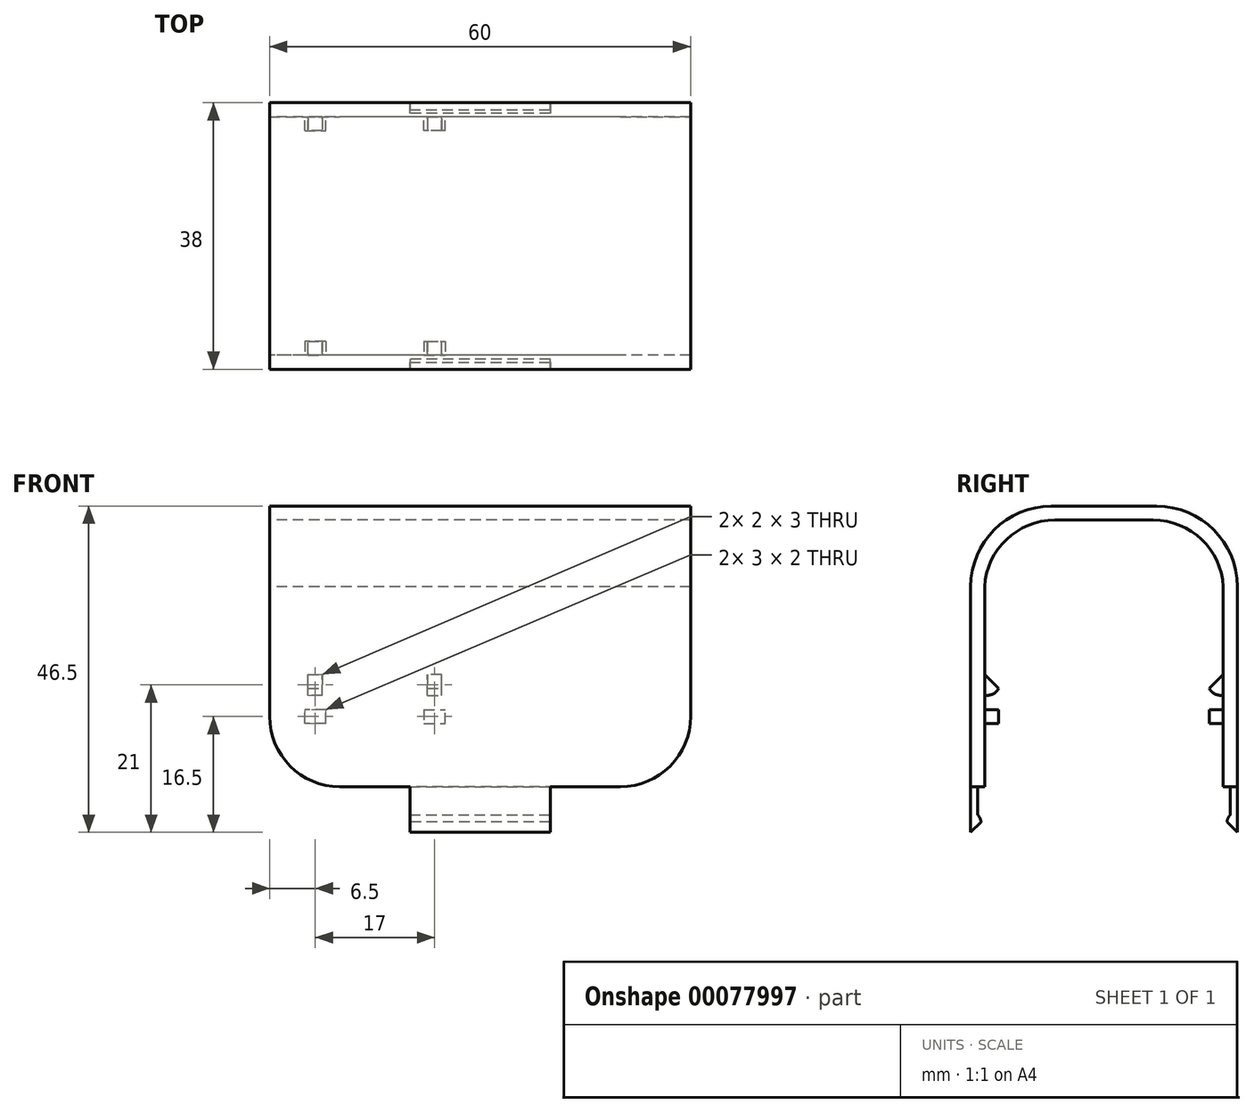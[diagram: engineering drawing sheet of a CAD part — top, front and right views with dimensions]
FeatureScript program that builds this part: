
annotation { "Feature Type Name" : "Feature", "Feature Type Description" : "" }
export const myFeature = defineFeature(function(context is Context, id is Id, definition is map)
    precondition{}
    {
        {
            var Q0;
            Q0=qCreatedBy(makeId("Right.planeOp"),FACE);
            var sketch = newSketch(context, id + "F0", { "sketchPlane" : qUnion([Q0])});
            skLineSegment(sketch, "E0", {"start": v(0, 0) * mm, "end": v(0, 28.5) * mm});
            skLineSegment(sketch, "E1", {"start": v(-11.5, 40) * mm, "end": v(-26.5, 40) * mm});
            skLineSegment(sketch, "E2", {"start": v(-38, 28.5) * mm, "end": v(-38, 0) * mm});
            skPoint(sketch, "E3.visualSharp", {"position": v(0, 40) * mm});
            skArc(sketch, "E3.filletArc", {"start": v(0, 28.5) * mm, "mid": v(-3.37, 36.63) * mm, "end": v(-11.5, 40) * mm});
            skPoint(sketch, "E4.visualSharp", {"position": v(-38, 40) * mm});
            skArc(sketch, "E4.filletArc", {"start": v(-26.5, 40) * mm, "mid": v(-34.63, 36.63) * mm, "end": v(-38, 28.5) * mm});
            skLineSegment(sketch, "E5.0", {"start": v(-36, 28.5) * mm, "end": v(-36, 0) * mm});
            skLineSegment(sketch, "E5.1", {"start": v(-2, 0) * mm, "end": v(-2, 28.5) * mm});
            skLineSegment(sketch, "E5.3", {"start": v(-11.99, 38) * mm, "end": v(-26.01, 38) * mm});
            skLineSegment(sketch, "E6", {"start": v(-38, 0) * mm, "end": v(-36, 0) * mm});
            skLineSegment(sketch, "E7", {"start": v(-2, 0) * mm, "end": v(0, 0) * mm});
            skArc(sketch, "E8", {"start": v(-2, 28.5) * mm, "mid": v(-5.1, 35.25) * mm, "end": v(-11.99, 38) * mm});
            skArc(sketch, "E9", {"start": v(-26.01, 38) * mm, "mid": v(-32.9, 35.25) * mm, "end": v(-36, 28.5) * mm});
            skSolve(sketch);
        }
        {
            var Q0;
            Q0=qSketchRegion(id+"F0",true);
            extrude(context, id + "F1", {"entities" : qUnion([Q0]), "endBound" : BoundingType.SYMMETRIC, "depth" : 60 * mm});
        }
        {
            var Q0;
            Q0=makeQuery(id+"F1.opExtrude","CAP_EDGE",EDGE,{"disambiguationData":[OSD([sQuery(id+"F0.wireOp",EDGE,"E6")])],"isStart":false});
            var Q1;
            Q1=makeQuery(id+"F1.opExtrude","CAP_EDGE",EDGE,{"disambiguationData":[OSD([sQuery(id+"F0.wireOp",EDGE,"E7")])],"isStart":false});
            var Q2;
            Q2=makeQuery(id+"F1.opExtrude","CAP_EDGE",EDGE,{"disambiguationData":[OSD([sQuery(id+"F0.wireOp",EDGE,"E7")])],"isStart":true});
            var Q3;
            Q3=makeQuery(id+"F1.opExtrude","CAP_EDGE",EDGE,{"disambiguationData":[OSD([sQuery(id+"F0.wireOp",EDGE,"E6")])],"isStart":true});
            fillet(context, id + "F2", {"entities" : qUnion([Q0, Q1, Q2, Q3]), "radius" : 10 * mm, "tangentPropagation" : true, "allowEdgeOverflow" : false});
        }
        {
            var Q0;
            Q0=makeQuery(id+"F1.opExtrude","SWEPT_FACE",FACE,{"disambiguationData":[OSD([sQuery(id+"F0.wireOp",EDGE,"E6")])]});
            var sketch = newSketch(context, id + "F3", { "sketchPlane" : qUnion([Q0])});
            skLineSegment(sketch, "E10", {"start": v(-20, 38) * mm, "end": v(-10, 38) * mm, "construction": true});
            skLineSegment(sketch, "E11", {"start": v(20, 38) * mm, "end": v(10, 38) * mm, "construction": true});
            skLineSegment(sketch, "E12", {"start": v(-10, 38) * mm, "end": v(-10, 0) * mm, "construction": true});
            skLineSegment(sketch, "E13", {"start": v(10, 38) * mm, "end": v(10, 0) * mm, "construction": true});
            skLineSegment(sketch, "E14", {"start": v(-10, 38) * mm, "end": v(10, 38) * mm});
            skLineSegment(sketch, "E15", {"start": v(-10, 0) * mm, "end": v(10, 0) * mm});
            skLineSegment(sketch, "E16", {"start": v(-10, 38) * mm, "end": v(-10, 37) * mm});
            skLineSegment(sketch, "E17", {"start": v(-10, 37) * mm, "end": v(10, 37) * mm});
            skLineSegment(sketch, "E18", {"start": v(10, 37) * mm, "end": v(10, 38) * mm});
            skLineSegment(sketch, "E19", {"start": v(-10, 0) * mm, "end": v(-10, 1) * mm});
            skLineSegment(sketch, "E20", {"start": v(-10, 1) * mm, "end": v(10, 1) * mm});
            skLineSegment(sketch, "E21", {"start": v(10, 1) * mm, "end": v(10, 0) * mm});
            skSolve(sketch);
        }
        {
            var Q0;
            Q0=makeQuery(id+"F3.imprint","IMPRINT",FACE,{"disambiguationData":[TD([[makeQuery(id+"F3.imprint","IMPRINT",EDGE,{"derivedFrom":sQuery(id+"F3.wireOp",EDGE,"E15")}),1.0]])]});
            var Q1;
            Q1=makeQuery(id+"F3.imprint","IMPRINT",FACE,{"disambiguationData":[TD([[makeQuery(id+"F3.imprint","IMPRINT",EDGE,{"derivedFrom":sQuery(id+"F3.wireOp",EDGE,"E14")}),1.0]])]});
            extrude(context, id + "F4", {"entities" : qUnion([Q0, Q1]), "operationType" : NewBodyOperationType.ADD, "depth" : 4 * mm});
        }
        {
            var Q0;
            Q0=makeQuery(id+"F4.opExtrude","CAP_FACE",FACE,{"disambiguationData":[OSD([sQuery(id+"F3.wireOp",EDGE,"E14"),sQuery(id+"F3.wireOp",EDGE,"E16"),sQuery(id+"F3.wireOp",EDGE,"E17"),sQuery(id+"F3.wireOp",EDGE,"E18")])],"isStart":false});
            var sketch = newSketch(context, id + "F5", { "sketchPlane" : qUnion([Q0])});
            skLineSegment(sketch, "E22", {"start": v(-10, 38) * mm, "end": v(-10, 36.5) * mm});
            skLineSegment(sketch, "E23", {"start": v(-10, 36.5) * mm, "end": v(9.99, 36.5) * mm});
            skLineSegment(sketch, "E24", {"start": v(9.99, 36.5) * mm, "end": v(10, 38) * mm});
            skLineSegment(sketch, "E25", {"start": v(-10, 38) * mm, "end": v(10, 38) * mm});
            skLineSegment(sketch, "E26.MirrorCS", {"start": v(-10, 0) * mm, "end": v(-10, 1.5) * mm});
            skLineSegment(sketch, "E27.MirrorCS", {"start": v(9.99, 1.5) * mm, "end": v(10, 0) * mm});
            skLineSegment(sketch, "E28.MirrorCS", {"start": v(-10, 1.5) * mm, "end": v(9.99, 1.5) * mm});
            skLineSegment(sketch, "E29.MirrorCS", {"start": v(-10, 0) * mm, "end": v(10, 0) * mm});
            skSolve(sketch);
        }
        {
            var Q0;
            Q0=qSketchRegion(id+"F5",true);
            extrude(context, id + "F6", {"entities" : qUnion([Q0]), "operationType" : NewBodyOperationType.ADD, "depth" : 3 * mm});
        }
        {
            var Q0;
            Q0=makeQuery(id+"F6.opExtrude","CAP_EDGE",EDGE,{"disambiguationData":[OSD([sQuery(id+"F5.wireOp",EDGE,"E28.MirrorCS")])],"isStart":true});
            var Q1;
            Q1=makeQuery(id+"F6.opExtrude","CAP_EDGE",EDGE,{"disambiguationData":[OSD([sQuery(id+"F5.wireOp",EDGE,"E23")])],"isStart":true});
            fillet(context, id + "F7", {"entities" : qUnion([Q0, Q1]), "radius" : 2 * mm, "tangentPropagation" : true, "allowEdgeOverflow" : false});
        }
        {
            var Q0;
            Q0=makeQuery(id+"F6.opExtrude","CAP_EDGE",EDGE,{"disambiguationData":[OSD([sQuery(id+"F5.wireOp",EDGE,"E28.MirrorCS")])],"isStart":false});
            var Q1;
            Q1=makeQuery(id+"F6.opExtrude","CAP_EDGE",EDGE,{"disambiguationData":[OSD([sQuery(id+"F5.wireOp",EDGE,"E23")])],"isStart":false});
            chamfer(context, id + "F8", {"entities" : qUnion([Q0, Q1]), "width" : 2 * mm, "tangentPropagation" : true});
        }
        {
            var Q0;
            Q0=makeQuery(id+"F1.opExtrude","SWEPT_FACE",FACE,{"disambiguationData":[OSD([sQuery(id+"F0.wireOp",EDGE,"E5.1")])]});
            var sketch = newSketch(context, id + "F9", { "sketchPlane" : qUnion([Q0])});
            skLineSegment(sketch, "E30", {"start": v(-20, 0) * mm, "end": v(-30, 0) * mm, "construction": true});
            skLineSegment(sketch, "E31", {"start": v(-25, 10) * mm, "end": v(-25, 11) * mm});
            skLineSegment(sketch, "E32", {"start": v(-25, 11) * mm, "end": v(-22, 11) * mm});
            skLineSegment(sketch, "E33", {"start": v(-25, 10) * mm, "end": v(-25, 9) * mm});
            skLineSegment(sketch, "E34", {"start": v(-25, 9) * mm, "end": v(-22, 9) * mm});
            skLineSegment(sketch, "E35", {"start": v(-22, 9) * mm, "end": v(-22, 11) * mm});
            skLineSegment(sketch, "E36", {"start": v(-25, 11) * mm, "end": v(-25, 13) * mm, "construction": true});
            skLineSegment(sketch, "E37", {"start": v(-30, 10) * mm, "end": v(-30, 6.48) * mm, "construction": true});
            skLineSegment(sketch, "E38", {"start": v(-24.5, 13) * mm, "end": v(-22.5, 13) * mm});
            skLineSegment(sketch, "E39", {"start": v(-22.5, 13) * mm, "end": v(-22.5, 16) * mm});
            skLineSegment(sketch, "E40", {"start": v(-22.5, 16) * mm, "end": v(-24.5, 16) * mm});
            skLineSegment(sketch, "E41", {"start": v(-24.5, 13) * mm, "end": v(-24.5, 16) * mm});
            skLineSegment(sketch, "E42", {"start": v(-25, 13) * mm, "end": v(-24.5, 13) * mm, "construction": true});
            skLineSegment(sketch, "E43", {"start": v(-15, 9) * mm, "end": v(-15, 3.17) * mm, "construction": true});
            skLineSegment(sketch, "E44.MirrorCS", {"start": v(-5, 11) * mm, "end": v(-5, 13) * mm, "construction": true});
            skLineSegment(sketch, "E45.MirrorCS", {"start": v(-5, 13) * mm, "end": v(-5.5, 13) * mm, "construction": true});
            skLineSegment(sketch, "E46.MirrorCS", {"start": v(-5, 10) * mm, "end": v(-5, 9) * mm});
            skLineSegment(sketch, "E47.MirrorCS", {"start": v(-5, 10) * mm, "end": v(-5, 11) * mm});
            skLineSegment(sketch, "E48.MirrorCS", {"start": v(-7.5, 16) * mm, "end": v(-5.5, 16) * mm});
            skLineSegment(sketch, "E49.MirrorCS", {"start": v(-5.5, 13) * mm, "end": v(-7.5, 13) * mm});
            skLineSegment(sketch, "E50.MirrorCS", {"start": v(-7.5, 13) * mm, "end": v(-7.5, 16) * mm});
            skLineSegment(sketch, "E51.MirrorCS", {"start": v(-5.5, 13) * mm, "end": v(-5.5, 16) * mm});
            skLineSegment(sketch, "E52.MirrorCS", {"start": v(-5, 11) * mm, "end": v(-8, 11) * mm});
            skLineSegment(sketch, "E53.MirrorCS", {"start": v(-5, 9) * mm, "end": v(-8, 9) * mm});
            skLineSegment(sketch, "E54.MirrorCS", {"start": v(-8, 9) * mm, "end": v(-8, 11) * mm});
            skSolve(sketch);
        }
        {
            var Q0;
            Q0=makeQuery(id+"F1.opExtrude","SWEPT_FACE",FACE,{"disambiguationData":[OSD([sQuery(id+"F0.wireOp",EDGE,"E5.0")])]});
            var sketch = newSketch(context, id + "F10", { "sketchPlane" : qUnion([Q0])});
            skLineSegment(sketch, "E55", {"start": v(30, 0) * mm, "end": v(20, 0) * mm, "construction": true});
            skLineSegment(sketch, "E56", {"start": v(22, 10) * mm, "end": v(22, 11) * mm});
            skLineSegment(sketch, "E57", {"start": v(22, 11) * mm, "end": v(25, 11) * mm});
            skLineSegment(sketch, "E58", {"start": v(22, 10) * mm, "end": v(22, 9) * mm});
            skLineSegment(sketch, "E59", {"start": v(22, 9) * mm, "end": v(25, 9) * mm});
            skLineSegment(sketch, "E60", {"start": v(25, 9) * mm, "end": v(25, 11) * mm});
            skLineSegment(sketch, "E61", {"start": v(22, 11) * mm, "end": v(22, 13) * mm, "construction": true});
            skLineSegment(sketch, "E62", {"start": v(22.5, 13) * mm, "end": v(24.5, 13) * mm});
            skLineSegment(sketch, "E63", {"start": v(24.5, 13) * mm, "end": v(24.5, 16) * mm});
            skLineSegment(sketch, "E64", {"start": v(24.5, 16) * mm, "end": v(22.5, 16) * mm});
            skLineSegment(sketch, "E65", {"start": v(22.5, 13) * mm, "end": v(22.5, 16) * mm});
            skLineSegment(sketch, "E66", {"start": v(22, 13) * mm, "end": v(22.5, 13) * mm, "construction": true});
            skLineSegment(sketch, "E67", {"start": v(20, 0) * mm, "end": v(30, 0) * mm, "construction": true});
            skLineSegment(sketch, "E68", {"start": v(30, 0) * mm, "end": v(30, 11) * mm, "construction": true});
            skLineSegment(sketch, "E69", {"start": v(30, 11) * mm, "end": v(25, 11) * mm, "construction": true});
            skLineSegment(sketch, "E70", {"start": v(15, 9) * mm, "end": v(15, 1.98) * mm, "construction": true});
            skLineSegment(sketch, "E71.MirrorCS", {"start": v(8, 11) * mm, "end": v(8, 13) * mm, "construction": true});
            skLineSegment(sketch, "E72.MirrorCS", {"start": v(8, 13) * mm, "end": v(7.5, 13) * mm, "construction": true});
            skLineSegment(sketch, "E73.MirrorCS", {"start": v(8, 10) * mm, "end": v(8, 9) * mm});
            skLineSegment(sketch, "E74.MirrorCS", {"start": v(8, 10) * mm, "end": v(8, 11) * mm});
            skLineSegment(sketch, "E75.MirrorCS", {"start": v(5.5, 13) * mm, "end": v(5.5, 16) * mm});
            skLineSegment(sketch, "E76.MirrorCS", {"start": v(7.5, 13) * mm, "end": v(7.5, 16) * mm});
            skLineSegment(sketch, "E77.MirrorCS", {"start": v(5.5, 16) * mm, "end": v(7.5, 16) * mm});
            skLineSegment(sketch, "E78.MirrorCS", {"start": v(7.5, 13) * mm, "end": v(5.5, 13) * mm});
            skLineSegment(sketch, "E79.MirrorCS", {"start": v(5, 9) * mm, "end": v(5, 11) * mm});
            skLineSegment(sketch, "E80.MirrorCS", {"start": v(8, 9) * mm, "end": v(5, 9) * mm});
            skLineSegment(sketch, "E81.MirrorCS", {"start": v(8, 11) * mm, "end": v(5, 11) * mm});
            skSolve(sketch);
        }
        {
            var Q0;
            Q0=makeQuery(id+"F9.imprint","IMPRINT",FACE,{"disambiguationData":[TD([[makeQuery(id+"F9.imprint","IMPRINT",EDGE,{"derivedFrom":sQuery(id+"F9.wireOp",EDGE,"E31")}),-1.0]])]});
            var Q1;
            Q1=makeQuery(id+"F9.imprint","IMPRINT",FACE,{"disambiguationData":[TD([[makeQuery(id+"F9.imprint","IMPRINT",EDGE,{"derivedFrom":sQuery(id+"F9.wireOp",EDGE,"E38")}),1.0]])]});
            var Q2;
            Q2=makeQuery(id+"F9.imprint","IMPRINT",FACE,{"disambiguationData":[TD([[makeQuery(id+"F9.imprint","IMPRINT",EDGE,{"derivedFrom":sQuery(id+"F9.wireOp",EDGE,"E46.MirrorCS")}),-1.0]])]});
            var Q3;
            Q3=makeQuery(id+"F9.imprint","IMPRINT",FACE,{"disambiguationData":[TD([[makeQuery(id+"F9.imprint","IMPRINT",EDGE,{"derivedFrom":sQuery(id+"F9.wireOp",EDGE,"E48.MirrorCS")}),-1.0]])]});
            extrude(context, id + "F11", {"entities" : qUnion([Q0, Q1, Q2, Q3]), "operationType" : NewBodyOperationType.ADD, "depth" : 2 * mm});
        }
        {
            var Q0;
            Q0=qSketchRegion(id+"F10",true);
            extrude(context, id + "F12", {"entities" : qUnion([Q0]), "operationType" : NewBodyOperationType.ADD, "depth" : 2 * mm});
        }
        {
            var Q0;
            Q0=makeQuery(id+"F11.opExtrude","CAP_EDGE",EDGE,{"disambiguationData":[OSD([sQuery(id+"F9.wireOp",EDGE,"E40")])],"isStart":false});
            var Q1;
            Q1=makeQuery(id+"F12.opExtrude","CAP_EDGE",EDGE,{"disambiguationData":[OSD([sQuery(id+"F10.wireOp",EDGE,"E64")])],"isStart":false});
            var Q2;
            Q2=makeQuery(id+"F11.opExtrude","CAP_EDGE",EDGE,{"disambiguationData":[OSD([sQuery(id+"F9.wireOp",EDGE,"E48.MirrorCS")])],"isStart":false});
            var Q3;
            Q3=makeQuery(id+"F12.opExtrude","CAP_EDGE",EDGE,{"disambiguationData":[OSD([sQuery(id+"F10.wireOp",EDGE,"E77.MirrorCS")])],"isStart":false});
            chamfer(context, id + "F13", {"entities" : qUnion([Q0, Q1, Q2, Q3]), "width" : 2 * mm, "tangentPropagation" : true});
        }
        {
            var Q0;
            Q0=makeQuery(id+"F11.opExtrude","CAP_EDGE",EDGE,{"disambiguationData":[OSD([sQuery(id+"F9.wireOp",EDGE,"E38")])],"isStart":false});
            var Q1;
            Q1=makeQuery(id+"F12.opExtrude","CAP_EDGE",EDGE,{"disambiguationData":[OSD([sQuery(id+"F10.wireOp",EDGE,"E62")])],"isStart":false});
            var Q2;
            Q2=makeQuery(id+"F11.opExtrude","CAP_EDGE",EDGE,{"disambiguationData":[OSD([sQuery(id+"F9.wireOp",EDGE,"E49.MirrorCS")])],"isStart":false});
            var Q3;
            Q3=makeQuery(id+"F12.opExtrude","CAP_EDGE",EDGE,{"disambiguationData":[OSD([sQuery(id+"F10.wireOp",EDGE,"E78.MirrorCS")])],"isStart":false});
            fillet(context, id + "F14", {"entities" : qUnion([Q0, Q1, Q2, Q3]), "radius" : 2 * mm, "tangentPropagation" : true, "allowEdgeOverflow" : false});
        }
    });
